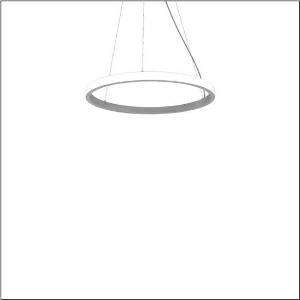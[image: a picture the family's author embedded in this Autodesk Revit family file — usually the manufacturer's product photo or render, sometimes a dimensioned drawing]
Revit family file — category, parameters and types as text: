
# Revit family: silica_21_ring-o_5pjbo2d1204a
name_source: partatom
category: Lighting Fixtures
units: mm (PartAtom-declared; Revit-internal decimal feet)

## family parameters
Cut with Voids When Loaded = No
Host = Face
Light Source = No
Part Type = Normal
Room Calculation Point = No
Round Connector Dimension = Use Diameter
Shared = No

## types (1)
- Silica 21 Ring-O (1 x LED, 4700 lm, 80 W, 3000K)
    Apparent Load = 80 VA
    CIE Flux Codes = 2 16 49 50 100
    Color Rendering = 80
    Color Temperature = 3000K
    Default Elevation = 1800 mm
    Description = Silica 21 Ring-O, suspended luminaire, of PMMA, frosted, light emission: outer ring side luminous distribution, primary light characteristic: symmetric, installation type: suspended mounting, LED, rated luminous flux: 4.700lm, luminous efficacy: 59lm/W, light colour: 830, colour temperature: 3000K, control gear: DALI 2, with terminal, 5-pole, mains connection: 230V, AC/DC, 0/50..60Hz, rated input power: 80W, housing, of extruded aluminium section, metallic grey (RAL 9006), diameter: 810mm, ceiling canopy, metallic grey (RAL 9006), protection rating (lamp compartment): IP40, insulation class (complete): insulation class I (protective earthing), certification: CE, impact resistance: IK02, permissible operating ambient temperature: 0..+35°C, packaging unit: 1 piece
    Height = 48 mm  [stored 0.15748 ft]
    Lamp = 1 x LED
    Lamp Light Flux = 4700 lm
    Lamp Power = 80 W
    Lamp count = 1
    Length = 810 mm
    Luminous efficacy = 59 lm/W
    Manufacturer = Siteco
    ModVariant = No
    Model = 5PJBO2D1204A
    Mounting Place = Ceiling
    Mounting Type = Pendant
    Number of Poles = 1
    OnlyDefault = Yes
    Power Factor = 1
    Product Name = Silica 21 Ring-O
    Product group = suspended luminaire
    ProductGroupID = 904
    Protection Class = Protection class I
    Protection Degree = IP 40
    RLX_Detail_Level = 1
    RLX_Emergency_Light_Flux = 0 lm
    RLX_Emergency_Type = 0
    RLX_Emergency_Type_DB = No
    RlxData = <blob elided: 13053 chars, md5=4ef031fb>
    Socket = socket
    Standby Power = 0 W
    System Light Flux = 4700 lm
    System Power = 80 W
    Type Comments = Product without accessories
    Type Image = l_1251760.jpg
    URL = http://relux.com
    VarID = ---
    Voltage = 0 V
    Weight = 0.00 kg
    Width = 0 mm  [stored 0 ft]

note: [stored X ft] marks values corroborated as IEEE doubles in the binary element streams (Revit-internal decimal feet)

## geometry (parser evidence)
native form markers: Sweep x10
no freeform markers — native parametric forms only
